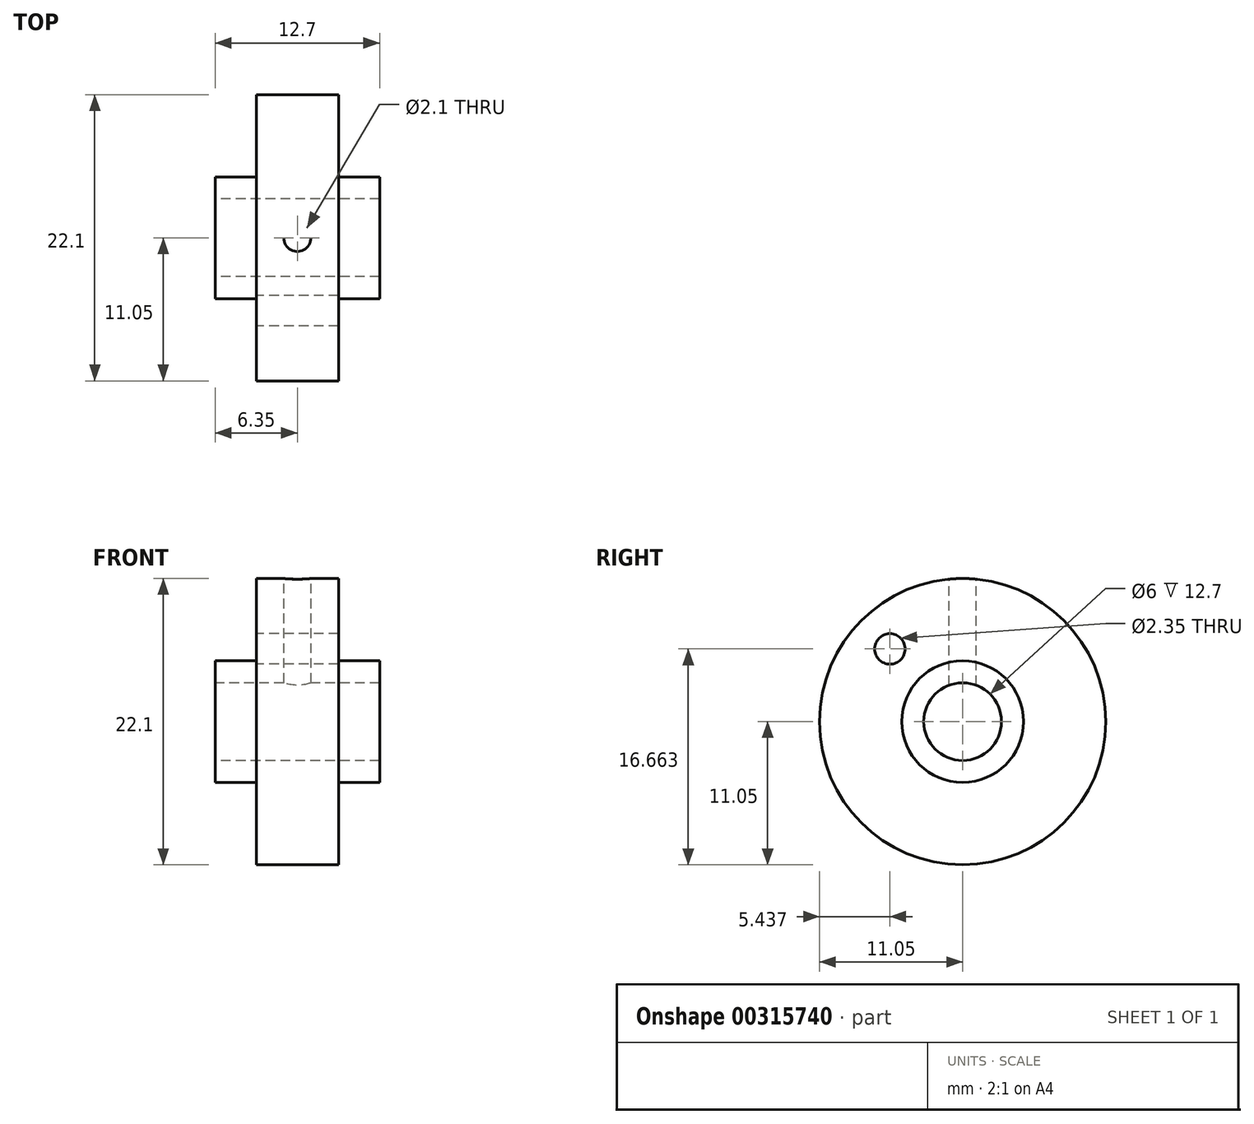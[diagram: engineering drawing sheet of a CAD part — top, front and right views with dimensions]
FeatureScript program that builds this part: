
annotation { "Feature Type Name" : "Feature", "Feature Type Description" : "" }
export const myFeature = defineFeature(function(context is Context, id is Id, definition is map)
    precondition{}
    {
        {
            var Q0;
            Q0=qCreatedBy(makeId("Front.planeOp"),FACE);
            var sketch = newSketch(context, id + "F0", { "sketchPlane" : qUnion([Q0])});
            skLineSegment(sketch, "E0", {"start": v(-6.35, 3) * mm, "end": v(6.35, 3) * mm});
            skLineSegment(sketch, "E1", {"start": v(6.35, 3) * mm, "end": v(6.35, 4.7) * mm});
            skLineSegment(sketch, "E2", {"start": v(6.35, 4.7) * mm, "end": v(3.18, 4.7) * mm});
            skLineSegment(sketch, "E3", {"start": v(3.18, 4.7) * mm, "end": v(3.18, 11.05) * mm});
            skLineSegment(sketch, "E4", {"start": v(3.18, 11.05) * mm, "end": v(-3.18, 11.05) * mm});
            skLineSegment(sketch, "E5", {"start": v(-3.18, 11.05) * mm, "end": v(-3.18, 4.7) * mm});
            skLineSegment(sketch, "E6", {"start": v(-3.17, 4.7) * mm, "end": v(-6.35, 4.7) * mm});
            skLineSegment(sketch, "E7", {"start": v(-6.35, 4.7) * mm, "end": v(-6.35, 3) * mm});
            skLineSegment(sketch, "E8", {"start": v(-6.35, 0) * mm, "end": v(6.35, 0) * mm, "construction": true});
            skPoint(sketch, "E9", {"position": v(0, 11.05) * mm});
            skSolve(sketch);
        }
        {
            var Q0;
            Q0 = qSketchRegion(id + "F0", true);
            var Q1;
            Q1=sQuery(id+"F0.wireOp",EDGE,"E8");
            revolve(context, id + "F1", {"entities" : qUnion([Q0]), "axis" : qUnion([Q1]), "revolveType" : RevolveType.FULL});
        }
        {
            var Q0;
            Q0=makeQuery(id+"F1.opRevolve","SWEPT_FACE",FACE,{"disambiguationData":[OSD([sQuery(id+"F0.wireOp",EDGE,"E5")])]});
            var sketch = newSketch(context, id + "F2", { "sketchPlane" : qUnion([Q0])});
            skLineSegment(sketch, "E10", {"start": v(0, 0) * mm, "end": v(5.61, 5.61) * mm, "construction": true});
            skSolve(sketch);
        }
        {
            var Q0;
            Q0=sQuery(id+"F2.wireOp",VERTEX,"E10.end");
            var Q1;
            Q1=makeQuery(id+"F1.opRevolve","SWEPT_BODY",BODY,{"disambiguationData":[OSD([sQuery(id+"F0.wireOp",EDGE,"E0"),sQuery(id+"F0.wireOp",EDGE,"E1"),sQuery(id+"F0.wireOp",EDGE,"E2"),sQuery(id+"F0.wireOp",EDGE,"E3"),sQuery(id+"F0.wireOp",EDGE,"E4"),sQuery(id+"F0.wireOp",EDGE,"E5"),sQuery(id+"F0.wireOp",EDGE,"E6"),sQuery(id+"F0.wireOp",EDGE,"E7")])]});
            hole(context, id + "F3", {"style" : HoleStyle.SIMPLE, "endStyle" : HoleEndStyle.THROUGH, "holeDiameter" : 2.35 * mm, "tappedDepth" : 4.2 * mm, "tapClearance" : 3, "locations" : qUnion([Q0]), "scope" : qUnion([Q1])});
        }
        {
            var Q0;
            Q0=sQuery(id+"F0.wireOp",EDGE,"E4");
            cPoint(context, id + "F4", {"entities" : qUnion([Q0]), "parameter" : 0.5});
        }
        {
            var Q0;
            Q0=qCreatedBy(makeId("Top.planeOp"),FACE);
            var Q1;
            Q1 = qCreatedBy(id + "F4" ,VERTEX);
            cPlane(context, id + "F5", {"entities" : qUnion([Q0, Q1]), "cplaneType" : CPlaneType.PLANE_POINT, "offset" : 25 * mm, "width" : 150 * mm, "height" : 150 * mm});
        }
        {
            var Q0;
            Q0=qCreatedBy(id+"F5.planeOp",FACE);
            var sketch = newSketch(context, id + "F6", { "sketchPlane" : qUnion([Q0])});
            skPoint(sketch, "E11", {"position": v(0, 0) * mm});
            skSolve(sketch);
        }
        {
            var Q0;
            Q0=sQuery(id+"F6.wireOp",VERTEX,"E11");
            var Q1;
            Q1=makeQuery(id+"F1.opRevolve","SWEPT_BODY",BODY,{"disambiguationData":[OSD([sQuery(id+"F0.wireOp",EDGE,"E0"),sQuery(id+"F0.wireOp",EDGE,"E1"),sQuery(id+"F0.wireOp",EDGE,"E2"),sQuery(id+"F0.wireOp",EDGE,"E3"),sQuery(id+"F0.wireOp",EDGE,"E4"),sQuery(id+"F0.wireOp",EDGE,"E5"),sQuery(id+"F0.wireOp",EDGE,"E6"),sQuery(id+"F0.wireOp",EDGE,"E7")])]});
            hole(context, id + "F7", {"style" : HoleStyle.SIMPLE, "endStyle" : HoleEndStyle.BLIND, "holeDiameter" : 2.1 * mm, "holeDepth" : 8.5 * mm, "tappedDepth" : 4.2 * mm, "tapClearance" : 3, "locations" : qUnion([Q0]), "scope" : qUnion([Q1])});
        }
    });
